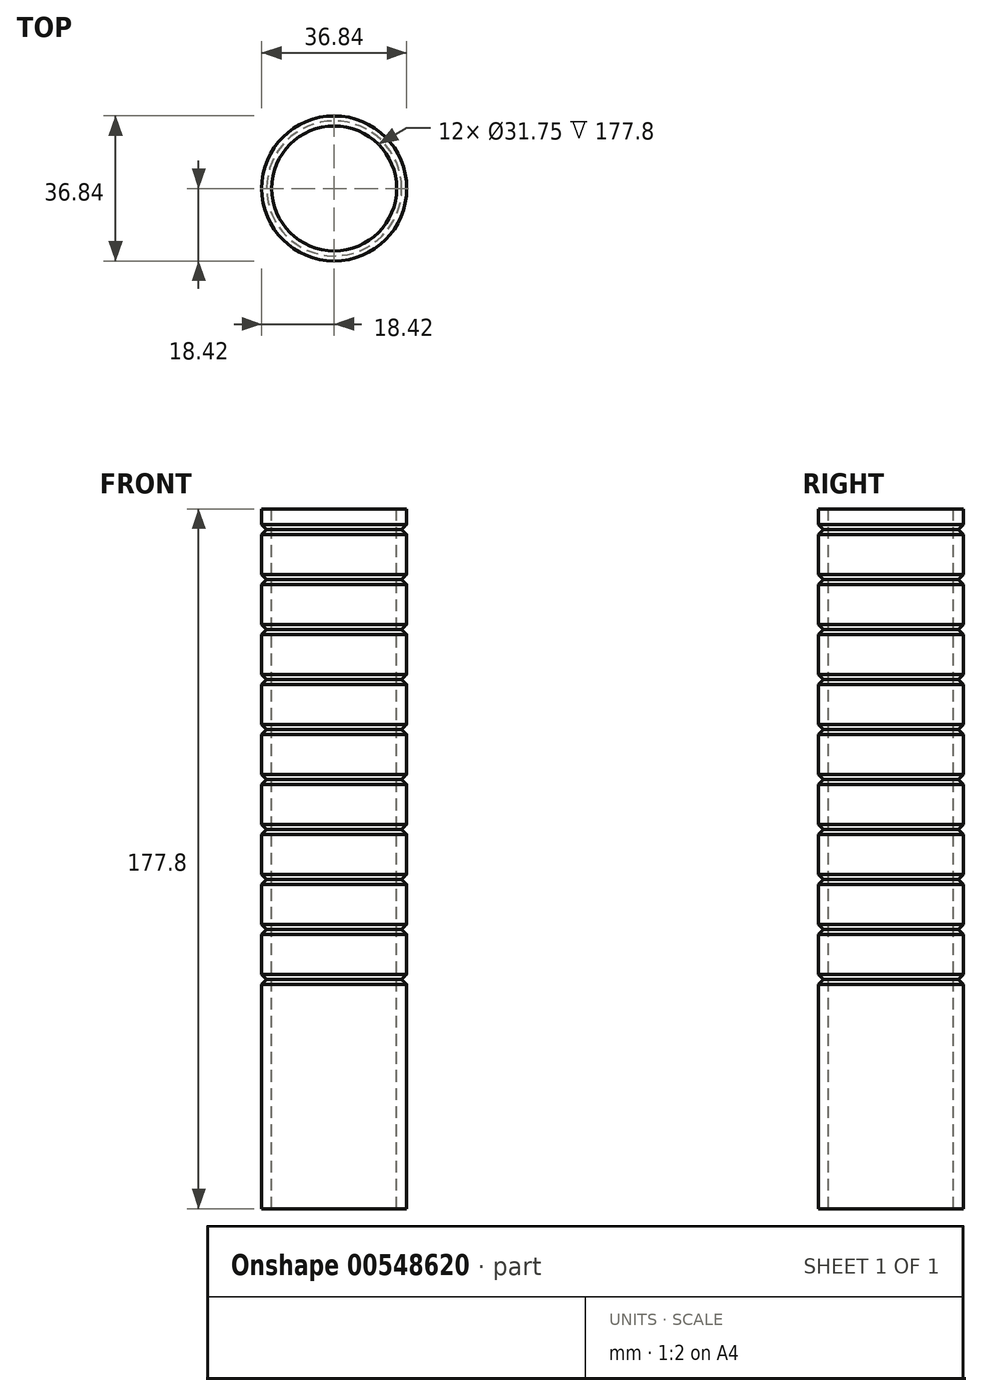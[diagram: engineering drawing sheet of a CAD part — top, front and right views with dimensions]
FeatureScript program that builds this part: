
annotation { "Feature Type Name" : "Feature", "Feature Type Description" : "" }
export const myFeature = defineFeature(function(context is Context, id is Id, definition is map)
    precondition{}
    {
        {
            var Q0;
            Q0=qCreatedBy(makeId("Front.planeOp"),FACE);
            var sketch = newSketch(context, id + "F0", { "sketchPlane" : qUnion([Q0])});
            skLineSegment(sketch, "E0", {"start": v(15.88, 84.72) * mm, "end": v(18.41, 84.72) * mm});
            skLineSegment(sketch, "E1", {"start": v(18.41, 84.72) * mm, "end": v(18.41, 80.75) * mm});
            skLineSegment(sketch, "E2", {"start": v(18.42, -93.08) * mm, "end": v(15.88, -93.08) * mm});
            skLineSegment(sketch, "E3", {"start": v(15.88, -93.08) * mm, "end": v(15.88, 84.72) * mm});
            skLineSegment(sketch, "E4", {"start": v(18.41, 78.2) * mm, "end": v(17.14, 79.48) * mm});
            skLineSegment(sketch, "E5", {"start": v(17.15, 79.48) * mm, "end": v(18.41, 80.75) * mm});
            skLineSegment(sketch, "E6.trimOffspring", {"start": v(18.41, 78.2) * mm, "end": v(18.41, 68.05) * mm});
            skLineSegment(sketch, "E7.1.0.0", {"start": v(17.15, 66.78) * mm, "end": v(18.42, 68.05) * mm});
            skLineSegment(sketch, "E7.1.0.1", {"start": v(18.42, 65.5) * mm, "end": v(17.15, 66.78) * mm});
            skLineSegment(sketch, "E7.2.0.0", {"start": v(17.15, 54.08) * mm, "end": v(18.42, 55.35) * mm});
            skLineSegment(sketch, "E7.2.0.1", {"start": v(18.42, 52.8) * mm, "end": v(17.15, 54.08) * mm});
            skLineSegment(sketch, "E7.3.0.0", {"start": v(17.15, 41.38) * mm, "end": v(18.42, 42.65) * mm});
            skLineSegment(sketch, "E7.3.0.1", {"start": v(18.42, 40.1) * mm, "end": v(17.15, 41.38) * mm});
            skLineSegment(sketch, "E7.4.0.0", {"start": v(17.15, 28.68) * mm, "end": v(18.42, 29.95) * mm});
            skLineSegment(sketch, "E7.4.0.1", {"start": v(18.42, 27.4) * mm, "end": v(17.14, 28.68) * mm});
            skLineSegment(sketch, "E7.5.0.0", {"start": v(17.15, 15.98) * mm, "end": v(18.42, 17.25) * mm});
            skLineSegment(sketch, "E7.5.0.1", {"start": v(18.42, 14.7) * mm, "end": v(17.15, 15.98) * mm});
            skLineSegment(sketch, "E7.6.0.0", {"start": v(17.15, 3.28) * mm, "end": v(18.42, 4.55) * mm});
            skLineSegment(sketch, "E7.6.0.1", {"start": v(18.41, 2) * mm, "end": v(17.14, 3.28) * mm});
            skLineSegment(sketch, "E7.7.0.0", {"start": v(17.15, -9.42) * mm, "end": v(18.42, -8.15) * mm});
            skLineSegment(sketch, "E7.7.0.1", {"start": v(18.41, -10.7) * mm, "end": v(17.14, -9.42) * mm});
            skLineSegment(sketch, "E7.8.0.0", {"start": v(17.14, -22.12) * mm, "end": v(18.41, -20.85) * mm});
            skLineSegment(sketch, "E7.8.0.1", {"start": v(18.41, -23.4) * mm, "end": v(17.14, -22.12) * mm});
            skLineSegment(sketch, "E7.9.0.0", {"start": v(17.14, -34.82) * mm, "end": v(18.41, -33.55) * mm});
            skLineSegment(sketch, "E7.9.0.1", {"start": v(18.41, -36.1) * mm, "end": v(17.14, -34.82) * mm});
            skLineSegment(sketch, "E7.direction1", {"start": v(17.14, 79.48) * mm, "end": v(17.14, 66.78) * mm, "construction": true});
            skLineSegment(sketch, "E8.trimOffspring", {"start": v(18.42, 65.5) * mm, "end": v(18.42, -93.08) * mm});
            skSolve(sketch);
        }
        {
            var Q0;
            Q0=qCreatedBy(makeId("Front.planeOp"),FACE);
            var sketch = newSketch(context, id + "F1", { "sketchPlane" : qUnion([Q0])});
            skLineSegment(sketch, "E9", {"start": v(0, 76.47) * mm, "end": v(0, -85.7) * mm});
            skSolve(sketch);
        }
        {
            var Q0;
            Q0=makeQuery(id+"F0.imprint","IMPRINT",FACE,{"disambiguationData":[TD([[makeQuery(id+"F0.imprint","IMPRINT",EDGE,{"derivedFrom":sQuery(id+"F0.wireOp",EDGE,"E0")}),-1.0]])]});
            var Q1;
            Q1=sQuery(id+"F1.wireOp",EDGE,"E9");
            revolve(context, id + "F2", {"entities" : qUnion([Q0]), "axis" : qUnion([Q1]), "revolveType" : RevolveType.FULL});
        }
    });
